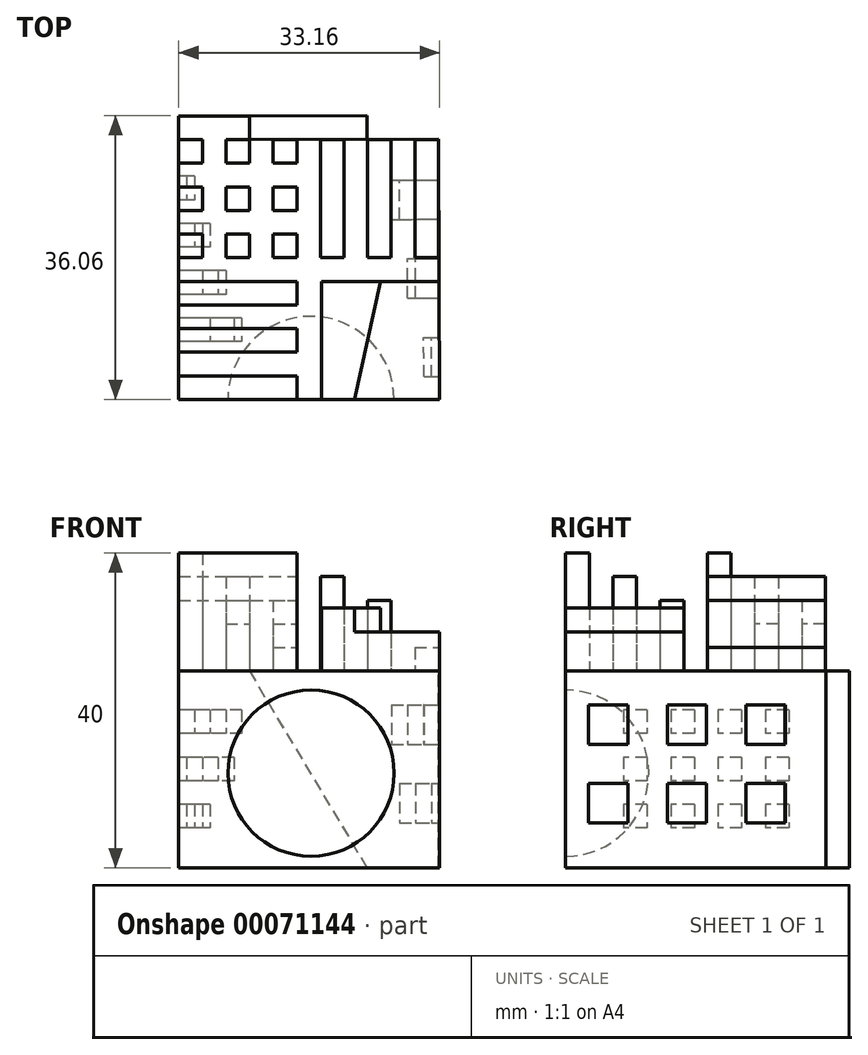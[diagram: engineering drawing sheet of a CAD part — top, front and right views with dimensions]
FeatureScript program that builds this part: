
annotation { "Feature Type Name" : "Feature", "Feature Type Description" : "" }
export const myFeature = defineFeature(function(context is Context, id is Id, definition is map)
    precondition{}
    {
        {
            var Q0;
            Q0=qCreatedBy(makeId("Top.planeOp"),FACE);
            var sketch = newSketch(context, id + "F0", { "sketchPlane" : qUnion([Q0])});
            skLineSegment(sketch, "E0.bottom", {"start": v(-18.94, 29.67) * mm, "end": v(-15.94, 29.67) * mm});
            skLineSegment(sketch, "E0.top", {"start": v(-18.94, 26.67) * mm, "end": v(-15.94, 26.67) * mm});
            skLineSegment(sketch, "E0.left", {"start": v(-18.94, 29.67) * mm, "end": v(-18.94, 26.67) * mm});
            skLineSegment(sketch, "E0.right", {"start": v(-15.94, 29.67) * mm, "end": v(-15.94, 26.67) * mm});
            skLineSegment(sketch, "E1.0.1.0", {"start": v(-18.94, 20.67) * mm, "end": v(-15.94, 20.67) * mm});
            skLineSegment(sketch, "E1.0.1.1", {"start": v(-18.94, 23.67) * mm, "end": v(-18.94, 20.67) * mm});
            skLineSegment(sketch, "E1.0.1.2", {"start": v(-15.94, 23.67) * mm, "end": v(-15.94, 20.67) * mm});
            skLineSegment(sketch, "E1.0.1.3", {"start": v(-18.94, 23.67) * mm, "end": v(-15.94, 23.67) * mm});
            skLineSegment(sketch, "E1.0.2.0", {"start": v(-18.94, 14.67) * mm, "end": v(-15.94, 14.67) * mm});
            skLineSegment(sketch, "E1.0.2.1", {"start": v(-18.94, 17.67) * mm, "end": v(-18.94, 14.67) * mm});
            skLineSegment(sketch, "E1.0.2.2", {"start": v(-15.94, 17.67) * mm, "end": v(-15.94, 14.67) * mm});
            skLineSegment(sketch, "E1.0.2.3", {"start": v(-18.94, 17.67) * mm, "end": v(-15.94, 17.67) * mm});
            skLineSegment(sketch, "E1.1.0.0", {"start": v(-12.94, 26.67) * mm, "end": v(-9.94, 26.67) * mm});
            skLineSegment(sketch, "E1.1.0.1", {"start": v(-12.94, 29.67) * mm, "end": v(-12.94, 26.67) * mm});
            skLineSegment(sketch, "E1.1.0.2", {"start": v(-9.94, 29.67) * mm, "end": v(-9.94, 26.67) * mm});
            skLineSegment(sketch, "E1.1.0.3", {"start": v(-12.94, 29.67) * mm, "end": v(-9.94, 29.67) * mm});
            skLineSegment(sketch, "E1.1.1.0", {"start": v(-12.94, 20.67) * mm, "end": v(-9.94, 20.67) * mm});
            skLineSegment(sketch, "E1.1.1.1", {"start": v(-12.94, 23.67) * mm, "end": v(-12.94, 20.67) * mm});
            skLineSegment(sketch, "E1.1.1.2", {"start": v(-9.94, 23.67) * mm, "end": v(-9.94, 20.67) * mm});
            skLineSegment(sketch, "E1.1.1.3", {"start": v(-12.94, 23.67) * mm, "end": v(-9.94, 23.67) * mm});
            skLineSegment(sketch, "E1.1.2.0", {"start": v(-12.94, 14.67) * mm, "end": v(-9.94, 14.67) * mm});
            skLineSegment(sketch, "E1.1.2.1", {"start": v(-12.94, 17.67) * mm, "end": v(-12.94, 14.67) * mm});
            skLineSegment(sketch, "E1.1.2.2", {"start": v(-9.94, 17.67) * mm, "end": v(-9.94, 14.67) * mm});
            skLineSegment(sketch, "E1.1.2.3", {"start": v(-12.94, 17.67) * mm, "end": v(-9.94, 17.67) * mm});
            skLineSegment(sketch, "E1.2.0.0", {"start": v(-6.94, 26.67) * mm, "end": v(-3.94, 26.67) * mm});
            skLineSegment(sketch, "E1.2.0.1", {"start": v(-6.94, 29.67) * mm, "end": v(-6.94, 26.67) * mm});
            skLineSegment(sketch, "E1.2.0.2", {"start": v(-3.94, 29.67) * mm, "end": v(-3.94, 26.67) * mm});
            skLineSegment(sketch, "E1.2.0.3", {"start": v(-6.94, 29.67) * mm, "end": v(-3.94, 29.67) * mm});
            skLineSegment(sketch, "E1.2.1.0", {"start": v(-6.94, 20.67) * mm, "end": v(-3.94, 20.67) * mm});
            skLineSegment(sketch, "E1.2.1.1", {"start": v(-6.94, 23.67) * mm, "end": v(-6.94, 20.67) * mm});
            skLineSegment(sketch, "E1.2.1.2", {"start": v(-3.94, 23.67) * mm, "end": v(-3.94, 20.67) * mm});
            skLineSegment(sketch, "E1.2.1.3", {"start": v(-6.94, 23.67) * mm, "end": v(-3.94, 23.67) * mm});
            skLineSegment(sketch, "E1.2.2.0", {"start": v(-6.94, 14.67) * mm, "end": v(-3.94, 14.67) * mm});
            skLineSegment(sketch, "E1.2.2.1", {"start": v(-6.94, 17.67) * mm, "end": v(-6.94, 14.67) * mm});
            skLineSegment(sketch, "E1.2.2.2", {"start": v(-3.94, 17.67) * mm, "end": v(-3.94, 14.67) * mm});
            skLineSegment(sketch, "E1.2.2.3", {"start": v(-6.94, 17.67) * mm, "end": v(-3.94, 17.67) * mm});
            skLineSegment(sketch, "E1.direction2", {"start": v(-18.94, 26.67) * mm, "end": v(-18.94, 20.67) * mm, "construction": true});
            skLineSegment(sketch, "E2.bottom", {"start": v(-0.94, 29.67) * mm, "end": v(2.06, 29.67) * mm});
            skLineSegment(sketch, "E2.top", {"start": v(-0.94, 14.67) * mm, "end": v(2.06, 14.67) * mm});
            skLineSegment(sketch, "E2.left", {"start": v(-0.94, 29.67) * mm, "end": v(-0.94, 14.67) * mm});
            skLineSegment(sketch, "E2.right", {"start": v(2.06, 29.67) * mm, "end": v(2.06, 14.67) * mm});
            skLineSegment(sketch, "E3.0.1.0", {"start": v(-0.94, 29.75) * mm, "end": v(2.06, 29.75) * mm});
            skLineSegment(sketch, "E3.0.1.1", {"start": v(-0.94, 29.75) * mm, "end": v(-0.94, 14.75) * mm});
            skLineSegment(sketch, "E3.0.1.2", {"start": v(2.06, 29.75) * mm, "end": v(2.06, 14.75) * mm});
            skLineSegment(sketch, "E3.1.0.0", {"start": v(5.06, 29.67) * mm, "end": v(8.06, 29.67) * mm});
            skLineSegment(sketch, "E3.1.0.1", {"start": v(5.06, 29.67) * mm, "end": v(5.06, 14.67) * mm});
            skLineSegment(sketch, "E3.1.0.2", {"start": v(8.06, 29.67) * mm, "end": v(8.06, 14.67) * mm});
            skLineSegment(sketch, "E3.1.0.3", {"start": v(5.06, 14.67) * mm, "end": v(8.06, 14.67) * mm});
            skLineSegment(sketch, "E3.1.1.0", {"start": v(5.06, 29.75) * mm, "end": v(8.06, 29.75) * mm});
            skLineSegment(sketch, "E3.1.1.1", {"start": v(5.06, 29.75) * mm, "end": v(5.06, 14.75) * mm});
            skLineSegment(sketch, "E3.1.1.2", {"start": v(8.06, 29.75) * mm, "end": v(8.06, 14.75) * mm});
            skLineSegment(sketch, "E3.2.0.0", {"start": v(11.06, 29.67) * mm, "end": v(14.06, 29.67) * mm});
            skLineSegment(sketch, "E3.2.0.1", {"start": v(11.06, 29.67) * mm, "end": v(11.06, 14.67) * mm});
            skLineSegment(sketch, "E3.2.0.2", {"start": v(14.06, 29.67) * mm, "end": v(14.06, 14.67) * mm});
            skLineSegment(sketch, "E3.2.0.3", {"start": v(11.06, 14.67) * mm, "end": v(14.06, 14.67) * mm});
            skLineSegment(sketch, "E3.2.1.0", {"start": v(11.06, 29.75) * mm, "end": v(14.06, 29.75) * mm});
            skLineSegment(sketch, "E3.2.1.1", {"start": v(11.06, 29.75) * mm, "end": v(11.06, 14.75) * mm});
            skLineSegment(sketch, "E3.2.1.2", {"start": v(14.06, 29.75) * mm, "end": v(14.06, 14.75) * mm});
            skLineSegment(sketch, "E3.direction1", {"start": v(-0.94, 29.67) * mm, "end": v(5.06, 29.67) * mm, "construction": true});
            skLineSegment(sketch, "E3.direction2", {"start": v(-0.94, 29.67) * mm, "end": v(-0.94, 29.75) * mm, "construction": true});
            skLineSegment(sketch, "E4.bottom", {"start": v(-18.94, 11.67) * mm, "end": v(-3.94, 11.67) * mm});
            skLineSegment(sketch, "E4.top", {"start": v(-18.94, 8.67) * mm, "end": v(-3.94, 8.67) * mm});
            skLineSegment(sketch, "E4.left", {"start": v(-18.94, 11.67) * mm, "end": v(-18.94, 8.67) * mm});
            skLineSegment(sketch, "E4.right", {"start": v(-3.94, 11.67) * mm, "end": v(-3.94, 8.67) * mm});
            skLineSegment(sketch, "E5.0.1.0", {"start": v(-18.94, 5.67) * mm, "end": v(-3.94, 5.67) * mm});
            skLineSegment(sketch, "E5.0.1.1", {"start": v(-18.94, 5.67) * mm, "end": v(-18.94, 2.67) * mm});
            skLineSegment(sketch, "E5.0.1.2", {"start": v(-18.94, 2.67) * mm, "end": v(-3.94, 2.67) * mm});
            skLineSegment(sketch, "E5.0.1.3", {"start": v(-3.94, 5.67) * mm, "end": v(-3.94, 2.67) * mm});
            skLineSegment(sketch, "E5.0.2.0", {"start": v(-18.94, -0.33) * mm, "end": v(-3.94, -0.33) * mm});
            skLineSegment(sketch, "E5.0.2.1", {"start": v(-18.94, -0.33) * mm, "end": v(-18.94, -3.33) * mm});
            skLineSegment(sketch, "E5.0.2.2", {"start": v(-18.94, -3.33) * mm, "end": v(-3.94, -3.33) * mm});
            skLineSegment(sketch, "E5.0.2.3", {"start": v(-3.94, -0.33) * mm, "end": v(-3.94, -3.33) * mm});
            skLineSegment(sketch, "E5.direction2", {"start": v(-18.94, 11.67) * mm, "end": v(-18.94, 5.67) * mm, "construction": true});
            skLineSegment(sketch, "E6.bottom", {"start": v(14.22, -3.33) * mm, "end": v(-0.78, -3.33) * mm});
            skLineSegment(sketch, "E6.top", {"start": v(14.22, 11.67) * mm, "end": v(-0.78, 11.67) * mm});
            skLineSegment(sketch, "E6.left", {"start": v(14.22, -3.33) * mm, "end": v(14.22, 11.67) * mm});
            skLineSegment(sketch, "E6.right", {"start": v(-0.78, -3.33) * mm, "end": v(-0.78, 11.67) * mm});
            skLineSegment(sketch, "E7", {"start": v(-18.94, 29.67) * mm, "end": v(14.06, 29.75) * mm});
            skLineSegment(sketch, "E8", {"start": v(14.06, 29.75) * mm, "end": v(14.22, -3.33) * mm});
            skLineSegment(sketch, "E9", {"start": v(14.22, -3.33) * mm, "end": v(-18.94, -3.33) * mm});
            skLineSegment(sketch, "E10", {"start": v(-18.94, 29.67) * mm, "end": v(-18.94, -3.33) * mm});
            skSolve(sketch);
        }
        {
            var Q0;
            {var subQ0=sQuery(id+"F0.wireOp",EDGE,"E6.right");Q0=makeQuery(id+"F0.imprint","IMPRINT",FACE,{"disambiguationData":[TD([[makeQuery(id+"F0.imprint","IMPRINT",EDGE,{"derivedFrom":subQ0}),-1.0]])]});}
            extrude(context, id + "F1", {"entities" : qUnion([Q0]), "depth" : 5 * mm});
        }
        {
            var Q0;
            {var subQ0=sQuery(id+"F0.wireOp",EDGE,"E5.0.2.0");Q0=makeQuery(id+"F0.imprint","IMPRINT",FACE,{"disambiguationData":[TD([[makeQuery(id+"F0.imprint","IMPRINT",EDGE,{"derivedFrom":subQ0}),-1.0]])]});}
            extrude(context, id + "F2", {"entities" : qUnion([Q0]), "depth" : 15 * mm});
        }
        {
            var Q0;
            Q0=makeQuery(id+"F0.imprint","IMPRINT",FACE,{"disambiguationData":[TD([[makeQuery(id+"F0.imprint","IMPRINT",EDGE,{"derivedFrom":sQuery(id+"F0.wireOp",EDGE,"E1.2.0.0")}),1.0]])]});
            extrude(context, id + "F3", {"entities" : qUnion([Q0]), "depth" : 3 * mm});
        }
        {
            var Q0;
            {var subQ2=sQuery(id+"F0.wireOp",EDGE,"E2.bottom");Q0=makeQuery(id+"F0.imprint","IMPRINT",FACE,{"disambiguationData":[TD([[makeQuery(id+"F0.imprint","IMPRINT",EDGE,{"derivedFrom":subQ2}),-1.0]])]});}
            extrude(context, id + "F4", {"entities" : qUnion([Q0]), "depth" : 12 * mm});
        }
        {
            var Q0;
            Q0=qCreatedBy(makeId("Top.planeOp"),FACE);
            var sketch = newSketch(context, id + "F5", { "sketchPlane" : qUnion([Q0])});
            skLineSegment(sketch, "E11.0", {"start": v(14.22, -3.33) * mm, "end": v(-18.94, -3.33) * mm});
            skLineSegment(sketch, "E12.0", {"start": v(-18.94, 29.67) * mm, "end": v(-18.94, -3.33) * mm});
            skLineSegment(sketch, "E13.0", {"start": v(14.06, 29.75) * mm, "end": v(14.22, -3.33) * mm});
            skLineSegment(sketch, "E14.0", {"start": v(-18.94, 29.67) * mm, "end": v(14.06, 29.75) * mm});
            skSolve(sketch);
        }
        {
            var Q0;
            Q0=makeQuery(id+"F5.imprint","IMPRINT",FACE,{"disambiguationData":[TD([[makeQuery(id+"F5.imprint","IMPRINT",EDGE,{"derivedFrom":sQuery(id+"F5.wireOp",EDGE,"E11.0")}),-1.0]])]});
            extrude(context, id + "F6", {"entities" : qUnion([Q0]), "oppositeDirection" : true, "depth" : 25 * mm});
        }
        {
            var Q0;
            Q0=makeQuery(id+"F6.opExtrude","SWEPT_FACE",FACE,{"disambiguationData":[OSD([sQuery(id+"F5.wireOp",EDGE,"E11.0")])]});
            var sketch = newSketch(context, id + "F7", { "sketchPlane" : qUnion([Q0])});
            skCircle(sketch, "E15", {"center": v(-2.12, -12.97) * mm, "radius": 10.56 * mm});
            skLineSegment(sketch, "E16", {"start": v(-2.12, -2.4) * mm, "end": v(-2.12, -23.53) * mm});
            skSolve(sketch);
        }
        {
            var Q0;
            {var subQ0=sQuery(id+"F7.wireOp",EDGE,"E16");Q0=makeQuery(id+"F7.imprint","IMPRINT",FACE,{"disambiguationData":[TD([[makeQuery(id+"F7.imprint","IMPRINT",EDGE,{"derivedFrom":subQ0}),-1.0]])]});}
            var Q1;
            Q1=sQuery(id+"F7.wireOp",EDGE,"E16");
            revolve(context, id + "F8", {"operationType" : NewBodyOperationType.REMOVE, "entities" : qUnion([Q0]), "axis" : qUnion([Q1]), "revolveType" : RevolveType.FULL, "oppositeDirection" : true});
        }
        {
            var Q0;
            Q0=makeQuery(id+"F6.opExtrude","SWEPT_FACE",FACE,{"disambiguationData":[OSD([sQuery(id+"F5.wireOp",EDGE,"E12.0")])]});
            var sketch = newSketch(context, id + "F9", { "sketchPlane" : qUnion([Q0])});
            skLineSegment(sketch, "E17.bottom", {"start": v(-25.02, -4.95) * mm, "end": v(-22.02, -4.95) * mm});
            skLineSegment(sketch, "E17.top", {"start": v(-25.02, -7.95) * mm, "end": v(-22.02, -7.95) * mm});
            skLineSegment(sketch, "E17.left", {"start": v(-25.02, -4.95) * mm, "end": v(-25.02, -7.95) * mm});
            skLineSegment(sketch, "E17.right", {"start": v(-22.02, -4.95) * mm, "end": v(-22.02, -7.95) * mm});
            skLineSegment(sketch, "E18.0.1.0", {"start": v(-25.02, -10.95) * mm, "end": v(-25.02, -13.95) * mm});
            skLineSegment(sketch, "E18.0.1.1", {"start": v(-25.02, -13.95) * mm, "end": v(-22.02, -13.95) * mm});
            skLineSegment(sketch, "E18.0.1.2", {"start": v(-25.02, -10.95) * mm, "end": v(-22.02, -10.95) * mm});
            skLineSegment(sketch, "E18.0.1.3", {"start": v(-22.02, -10.95) * mm, "end": v(-22.02, -13.95) * mm});
            skLineSegment(sketch, "E18.0.2.0", {"start": v(-25.02, -16.95) * mm, "end": v(-25.02, -19.95) * mm});
            skLineSegment(sketch, "E18.0.2.1", {"start": v(-25.02, -19.95) * mm, "end": v(-22.02, -19.95) * mm});
            skLineSegment(sketch, "E18.0.2.2", {"start": v(-25.02, -16.95) * mm, "end": v(-22.02, -16.95) * mm});
            skLineSegment(sketch, "E18.0.2.3", {"start": v(-22.02, -16.95) * mm, "end": v(-22.02, -19.95) * mm});
            skLineSegment(sketch, "E18.1.0.0", {"start": v(-19.02, -4.95) * mm, "end": v(-19.02, -7.95) * mm});
            skLineSegment(sketch, "E18.1.0.1", {"start": v(-19.02, -7.95) * mm, "end": v(-16.02, -7.95) * mm});
            skLineSegment(sketch, "E18.1.0.2", {"start": v(-19.02, -4.95) * mm, "end": v(-16.02, -4.95) * mm});
            skLineSegment(sketch, "E18.1.0.3", {"start": v(-16.02, -4.95) * mm, "end": v(-16.02, -7.95) * mm});
            skLineSegment(sketch, "E18.1.1.0", {"start": v(-19.02, -10.95) * mm, "end": v(-19.02, -13.95) * mm});
            skLineSegment(sketch, "E18.1.1.1", {"start": v(-19.02, -13.95) * mm, "end": v(-16.02, -13.95) * mm});
            skLineSegment(sketch, "E18.1.1.2", {"start": v(-19.02, -10.95) * mm, "end": v(-16.02, -10.95) * mm});
            skLineSegment(sketch, "E18.1.1.3", {"start": v(-16.02, -10.95) * mm, "end": v(-16.02, -13.95) * mm});
            skLineSegment(sketch, "E18.1.2.0", {"start": v(-19.02, -16.95) * mm, "end": v(-19.02, -19.95) * mm});
            skLineSegment(sketch, "E18.1.2.1", {"start": v(-19.02, -19.95) * mm, "end": v(-16.02, -19.95) * mm});
            skLineSegment(sketch, "E18.1.2.2", {"start": v(-19.02, -16.95) * mm, "end": v(-16.02, -16.95) * mm});
            skLineSegment(sketch, "E18.1.2.3", {"start": v(-16.02, -16.95) * mm, "end": v(-16.02, -19.95) * mm});
            skLineSegment(sketch, "E18.2.0.0", {"start": v(-13.02, -4.95) * mm, "end": v(-13.02, -7.95) * mm});
            skLineSegment(sketch, "E18.2.0.1", {"start": v(-13.02, -7.95) * mm, "end": v(-10.02, -7.95) * mm});
            skLineSegment(sketch, "E18.2.0.2", {"start": v(-13.02, -4.95) * mm, "end": v(-10.02, -4.95) * mm});
            skLineSegment(sketch, "E18.2.0.3", {"start": v(-10.02, -4.95) * mm, "end": v(-10.02, -7.95) * mm});
            skLineSegment(sketch, "E18.2.1.0", {"start": v(-13.02, -10.95) * mm, "end": v(-13.02, -13.95) * mm});
            skLineSegment(sketch, "E18.2.1.1", {"start": v(-13.02, -13.95) * mm, "end": v(-10.02, -13.95) * mm});
            skLineSegment(sketch, "E18.2.1.2", {"start": v(-13.02, -10.95) * mm, "end": v(-10.02, -10.95) * mm});
            skLineSegment(sketch, "E18.2.1.3", {"start": v(-10.02, -10.95) * mm, "end": v(-10.02, -13.95) * mm});
            skLineSegment(sketch, "E18.2.2.0", {"start": v(-13.02, -16.95) * mm, "end": v(-13.02, -19.95) * mm});
            skLineSegment(sketch, "E18.2.2.1", {"start": v(-13.02, -19.95) * mm, "end": v(-10.02, -19.95) * mm});
            skLineSegment(sketch, "E18.2.2.2", {"start": v(-13.02, -16.95) * mm, "end": v(-10.02, -16.95) * mm});
            skLineSegment(sketch, "E18.2.2.3", {"start": v(-10.02, -16.95) * mm, "end": v(-10.02, -19.95) * mm});
            skLineSegment(sketch, "E18.3.0.0", {"start": v(-7.02, -4.95) * mm, "end": v(-7.02, -7.95) * mm});
            skLineSegment(sketch, "E18.3.0.1", {"start": v(-7.02, -7.95) * mm, "end": v(-4.02, -7.95) * mm});
            skLineSegment(sketch, "E18.3.0.2", {"start": v(-7.02, -4.95) * mm, "end": v(-4.02, -4.95) * mm});
            skLineSegment(sketch, "E18.3.0.3", {"start": v(-4.02, -4.95) * mm, "end": v(-4.02, -7.95) * mm});
            skLineSegment(sketch, "E18.3.1.0", {"start": v(-7.02, -10.95) * mm, "end": v(-7.02, -13.95) * mm});
            skLineSegment(sketch, "E18.3.1.1", {"start": v(-7.02, -13.95) * mm, "end": v(-4.02, -13.95) * mm});
            skLineSegment(sketch, "E18.3.1.2", {"start": v(-7.02, -10.95) * mm, "end": v(-4.02, -10.95) * mm});
            skLineSegment(sketch, "E18.3.1.3", {"start": v(-4.02, -10.95) * mm, "end": v(-4.02, -13.95) * mm});
            skLineSegment(sketch, "E18.3.2.0", {"start": v(-7.02, -16.95) * mm, "end": v(-7.02, -19.95) * mm});
            skLineSegment(sketch, "E18.3.2.1", {"start": v(-7.02, -19.95) * mm, "end": v(-4.02, -19.95) * mm});
            skLineSegment(sketch, "E18.3.2.2", {"start": v(-7.02, -16.95) * mm, "end": v(-4.02, -16.95) * mm});
            skLineSegment(sketch, "E18.3.2.3", {"start": v(-4.02, -16.95) * mm, "end": v(-4.02, -19.95) * mm});
            skLineSegment(sketch, "E18.direction1", {"start": v(-25.02, -7.95) * mm, "end": v(-19.02, -7.95) * mm, "construction": true});
            skLineSegment(sketch, "E18.direction2", {"start": v(-25.02, -7.95) * mm, "end": v(-25.02, -13.95) * mm, "construction": true});
            skSolve(sketch);
        }
        {
            var Q0;
            Q0=makeQuery(id+"F6.opExtrude","SWEPT_FACE",FACE,{"disambiguationData":[OSD([sQuery(id+"F5.wireOp",EDGE,"E13.0")])]});
            var sketch = newSketch(context, id + "F10", { "sketchPlane" : qUnion([Q0])});
            skLineSegment(sketch, "E19.bottom", {"start": v(-0.5, -4.3) * mm, "end": v(4.5, -4.3) * mm});
            skLineSegment(sketch, "E19.top", {"start": v(-0.5, -9.3) * mm, "end": v(4.5, -9.3) * mm});
            skLineSegment(sketch, "E19.left", {"start": v(-0.5, -4.3) * mm, "end": v(-0.5, -9.3) * mm});
            skLineSegment(sketch, "E19.right", {"start": v(4.5, -4.3) * mm, "end": v(4.5, -9.3) * mm});
            skLineSegment(sketch, "E20.0.1.0", {"start": v(-0.5, -14.3) * mm, "end": v(4.5, -14.3) * mm});
            skLineSegment(sketch, "E20.0.1.1", {"start": v(-0.5, -19.3) * mm, "end": v(4.5, -19.3) * mm});
            skLineSegment(sketch, "E20.0.1.2", {"start": v(4.5, -14.3) * mm, "end": v(4.5, -19.3) * mm});
            skLineSegment(sketch, "E20.0.1.3", {"start": v(-0.5, -14.3) * mm, "end": v(-0.5, -19.3) * mm});
            skLineSegment(sketch, "E20.1.0.0", {"start": v(9.5, -4.3) * mm, "end": v(14.5, -4.3) * mm});
            skLineSegment(sketch, "E20.1.0.1", {"start": v(9.5, -9.3) * mm, "end": v(14.5, -9.3) * mm});
            skLineSegment(sketch, "E20.1.0.2", {"start": v(14.5, -4.3) * mm, "end": v(14.5, -9.3) * mm});
            skLineSegment(sketch, "E20.1.0.3", {"start": v(9.5, -4.3) * mm, "end": v(9.5, -9.3) * mm});
            skLineSegment(sketch, "E20.1.1.0", {"start": v(9.5, -14.3) * mm, "end": v(14.5, -14.3) * mm});
            skLineSegment(sketch, "E20.1.1.1", {"start": v(9.5, -19.3) * mm, "end": v(14.5, -19.3) * mm});
            skLineSegment(sketch, "E20.1.1.2", {"start": v(14.5, -14.3) * mm, "end": v(14.5, -19.3) * mm});
            skLineSegment(sketch, "E20.1.1.3", {"start": v(9.5, -14.3) * mm, "end": v(9.5, -19.3) * mm});
            skLineSegment(sketch, "E20.2.0.0", {"start": v(19.5, -4.3) * mm, "end": v(24.5, -4.3) * mm});
            skLineSegment(sketch, "E20.2.0.1", {"start": v(19.5, -9.3) * mm, "end": v(24.5, -9.3) * mm});
            skLineSegment(sketch, "E20.2.0.2", {"start": v(24.5, -4.3) * mm, "end": v(24.5, -9.3) * mm});
            skLineSegment(sketch, "E20.2.0.3", {"start": v(19.5, -4.3) * mm, "end": v(19.5, -9.3) * mm});
            skLineSegment(sketch, "E20.2.1.0", {"start": v(19.5, -14.3) * mm, "end": v(24.5, -14.3) * mm});
            skLineSegment(sketch, "E20.2.1.1", {"start": v(19.5, -19.3) * mm, "end": v(24.5, -19.3) * mm});
            skLineSegment(sketch, "E20.2.1.2", {"start": v(24.5, -14.3) * mm, "end": v(24.5, -19.3) * mm});
            skLineSegment(sketch, "E20.2.1.3", {"start": v(19.5, -14.3) * mm, "end": v(19.5, -19.3) * mm});
            skLineSegment(sketch, "E20.direction1", {"start": v(-0.5, -4.3) * mm, "end": v(9.5, -4.3) * mm, "construction": true});
            skLineSegment(sketch, "E20.direction2", {"start": v(-0.5, -4.3) * mm, "end": v(-0.5, -14.3) * mm, "construction": true});
            skSolve(sketch);
        }
        {
            var Q0;
            Q0=makeQuery(id+"F10.imprint","IMPRINT",FACE,{"disambiguationData":[TD([[makeQuery(id+"F10.imprint","IMPRINT",EDGE,{"derivedFrom":sQuery(id+"F10.wireOp",EDGE,"E19.bottom")}),-1.0]])]});
            extrude(context, id + "F11", {"entities" : qUnion([Q0]), "operationType" : NewBodyOperationType.REMOVE, "oppositeDirection" : true, "depth" : 2 * mm});
        }
        {
            var Q0;
            {var subQ0=sQuery(id+"F0.wireOp",EDGE,"E5.0.1.0");Q0=makeQuery(id+"F0.imprint","IMPRINT",FACE,{"disambiguationData":[TD([[makeQuery(id+"F0.imprint","IMPRINT",EDGE,{"derivedFrom":subQ0}),-1.0]])]});}
            extrude(context, id + "F12", {"entities" : qUnion([Q0]), "operationType" : NewBodyOperationType.ADD, "depth" : 12 * mm});
        }
        {
            var Q0;
            {var subQ0=sQuery(id+"F0.wireOp",EDGE,"E4.bottom");Q0=makeQuery(id+"F0.imprint","IMPRINT",FACE,{"disambiguationData":[TD([[makeQuery(id+"F0.imprint","IMPRINT",EDGE,{"derivedFrom":subQ0}),-1.0]])]});}
            extrude(context, id + "F13", {"entities" : qUnion([Q0]), "operationType" : NewBodyOperationType.ADD, "depth" : 9 * mm});
        }
        {
            var Q0;
            Q0=makeQuery(id+"F0.imprint","IMPRINT",FACE,{"disambiguationData":[TD([[makeQuery(id+"F0.imprint","IMPRINT",EDGE,{"derivedFrom":sQuery(id+"F0.wireOp",EDGE,"E1.1.0.0")}),1.0]])]});
            extrude(context, id + "F14", {"entities" : qUnion([Q0]), "operationType" : NewBodyOperationType.ADD, "depth" : 6 * mm});
        }
        {
            var Q0;
            {var subQ0=sQuery(id+"F0.wireOp",EDGE,"E0.bottom");Q0=makeQuery(id+"F0.imprint","IMPRINT",FACE,{"disambiguationData":[TD([[makeQuery(id+"F0.imprint","IMPRINT",EDGE,{"derivedFrom":subQ0}),-1.0]])]});}
            extrude(context, id + "F15", {"entities" : qUnion([Q0]), "operationType" : NewBodyOperationType.ADD, "depth" : 9 * mm});
        }
        {
            var Q0;
            Q0=makeQuery(id+"F0.imprint","IMPRINT",FACE,{"disambiguationData":[TD([[makeQuery(id+"F0.imprint","IMPRINT",EDGE,{"derivedFrom":sQuery(id+"F0.wireOp",EDGE,"E1.1.1.0")}),1.0]])]});
            extrude(context, id + "F16", {"entities" : qUnion([Q0]), "operationType" : NewBodyOperationType.ADD, "depth" : 9 * mm});
        }
        {
            var Q0;
            {var subQ0=sQuery(id+"F0.wireOp",EDGE,"E1.0.2.0");Q0=makeQuery(id+"F0.imprint","IMPRINT",FACE,{"disambiguationData":[TD([[makeQuery(id+"F0.imprint","IMPRINT",EDGE,{"derivedFrom":subQ0}),1.0]])]});}
            extrude(context, id + "F17", {"entities" : qUnion([Q0]), "operationType" : NewBodyOperationType.ADD, "depth" : 15 * mm});
        }
        {
            var Q0;
            {var subQ0=sQuery(id+"F0.wireOp",EDGE,"E1.0.1.0");Q0=makeQuery(id+"F0.imprint","IMPRINT",FACE,{"disambiguationData":[TD([[makeQuery(id+"F0.imprint","IMPRINT",EDGE,{"derivedFrom":subQ0}),1.0]])]});}
            extrude(context, id + "F18", {"entities" : qUnion([Q0]), "operationType" : NewBodyOperationType.ADD, "depth" : 12 * mm});
        }
        {
            var Q0;
            Q0=makeQuery(id+"F0.imprint","IMPRINT",FACE,{"disambiguationData":[TD([[makeQuery(id+"F0.imprint","IMPRINT",EDGE,{"derivedFrom":sQuery(id+"F0.wireOp",EDGE,"E1.2.1.0")}),1.0]])]});
            extrude(context, id + "F19", {"entities" : qUnion([Q0]), "operationType" : NewBodyOperationType.ADD, "depth" : 6 * mm});
        }
        {
            var Q0;
            Q0=makeQuery(id+"F0.imprint","IMPRINT",FACE,{"disambiguationData":[TD([[makeQuery(id+"F0.imprint","IMPRINT",EDGE,{"derivedFrom":sQuery(id+"F0.wireOp",EDGE,"E1.2.2.0")}),1.0]])]});
            extrude(context, id + "F20", {"entities" : qUnion([Q0]), "operationType" : NewBodyOperationType.ADD, "depth" : 9 * mm});
        }
        {
            var Q0;
            Q0=makeQuery(id+"F0.imprint","IMPRINT",FACE,{"disambiguationData":[TD([[makeQuery(id+"F0.imprint","IMPRINT",EDGE,{"derivedFrom":sQuery(id+"F0.wireOp",EDGE,"E1.1.2.0")}),1.0]])]});
            extrude(context, id + "F21", {"entities" : qUnion([Q0]), "operationType" : NewBodyOperationType.ADD, "depth" : 12 * mm});
        }
        {
            var Q0;
            {var subQ1=sQuery(id+"F0.wireOp",EDGE,"E3.1.0.0");Q0=makeQuery(id+"F0.imprint","IMPRINT",FACE,{"disambiguationData":[TD([[makeQuery(id+"F0.imprint","IMPRINT",EDGE,{"derivedFrom":subQ1}),-1.0]])]});}
            extrude(context, id + "F22", {"entities" : qUnion([Q0]), "operationType" : NewBodyOperationType.ADD, "depth" : 9 * mm});
        }
        {
            var Q0;
            {var subQ2=sQuery(id+"F0.wireOp",EDGE,"E3.2.0.0");Q0=makeQuery(id+"F0.imprint","IMPRINT",FACE,{"disambiguationData":[TD([[makeQuery(id+"F0.imprint","IMPRINT",EDGE,{"derivedFrom":subQ2}),-1.0]])]});}
            extrude(context, id + "F23", {"entities" : qUnion([Q0]), "operationType" : NewBodyOperationType.ADD, "depth" : 3 * mm});
        }
        {
            var Q0;
            Q0=makeQuery(id+"F10.imprint","IMPRINT",FACE,{"disambiguationData":[TD([[makeQuery(id+"F10.imprint","IMPRINT",EDGE,{"derivedFrom":sQuery(id+"F10.wireOp",EDGE,"E20.1.0.0")}),-1.0]])]});
            extrude(context, id + "F24", {"entities" : qUnion([Q0]), "operationType" : NewBodyOperationType.REMOVE, "oppositeDirection" : true, "depth" : 4 * mm});
        }
        {
            var Q0;
            Q0=makeQuery(id+"F10.imprint","IMPRINT",FACE,{"disambiguationData":[TD([[makeQuery(id+"F10.imprint","IMPRINT",EDGE,{"derivedFrom":sQuery(id+"F10.wireOp",EDGE,"E20.2.0.0")}),-1.0]])]});
            extrude(context, id + "F25", {"entities" : qUnion([Q0]), "operationType" : NewBodyOperationType.REMOVE, "oppositeDirection" : true, "depth" : 6 * mm});
        }
        {
            var Q0;
            Q0=makeQuery(id+"F10.imprint","IMPRINT",FACE,{"disambiguationData":[TD([[makeQuery(id+"F10.imprint","IMPRINT",EDGE,{"derivedFrom":sQuery(id+"F10.wireOp",EDGE,"E20.0.1.0")}),-1.0]])]});
            extrude(context, id + "F26", {"entities" : qUnion([Q0]), "operationType" : NewBodyOperationType.REMOVE, "oppositeDirection" : true, "depth" : 1 * mm});
        }
        {
            var Q0;
            Q0=makeQuery(id+"F10.imprint","IMPRINT",FACE,{"disambiguationData":[TD([[makeQuery(id+"F10.imprint","IMPRINT",EDGE,{"derivedFrom":sQuery(id+"F10.wireOp",EDGE,"E20.1.1.0")}),-1.0]])]});
            extrude(context, id + "F27", {"entities" : qUnion([Q0]), "operationType" : NewBodyOperationType.REMOVE, "oppositeDirection" : true, "depth" : 3 * mm});
        }
        {
            var Q0;
            Q0=makeQuery(id+"F10.imprint","IMPRINT",FACE,{"disambiguationData":[TD([[makeQuery(id+"F10.imprint","IMPRINT",EDGE,{"derivedFrom":sQuery(id+"F10.wireOp",EDGE,"E20.2.1.0")}),-1.0]])]});
            extrude(context, id + "F28", {"entities" : qUnion([Q0]), "operationType" : NewBodyOperationType.REMOVE, "oppositeDirection" : true, "depth" : 5 * mm});
        }
        {
            var Q0;
            Q0=makeQuery(id+"F9.imprint","IMPRINT",FACE,{"disambiguationData":[TD([[makeQuery(id+"F9.imprint","IMPRINT",EDGE,{"derivedFrom":sQuery(id+"F9.wireOp",EDGE,"E17.bottom")}),-1.0]])]});
            extrude(context, id + "F29", {"entities" : qUnion([Q0]), "operationType" : NewBodyOperationType.REMOVE, "oppositeDirection" : true, "depth" : 2 * mm});
        }
        {
            var Q0;
            Q0=makeQuery(id+"F9.imprint","IMPRINT",FACE,{"disambiguationData":[TD([[makeQuery(id+"F9.imprint","IMPRINT",EDGE,{"derivedFrom":sQuery(id+"F9.wireOp",EDGE,"E18.1.0.0")}),1.0]])]});
            extrude(context, id + "F30", {"entities" : qUnion([Q0]), "operationType" : NewBodyOperationType.REMOVE, "oppositeDirection" : true, "depth" : 4 * mm});
        }
        {
            var Q0;
            Q0=makeQuery(id+"F9.imprint","IMPRINT",FACE,{"disambiguationData":[TD([[makeQuery(id+"F9.imprint","IMPRINT",EDGE,{"derivedFrom":sQuery(id+"F9.wireOp",EDGE,"E18.2.0.0")}),1.0]])]});
            extrude(context, id + "F31", {"entities" : qUnion([Q0]), "operationType" : NewBodyOperationType.REMOVE, "oppositeDirection" : true, "depth" : 6 * mm});
        }
        {
            var Q0;
            Q0=makeQuery(id+"F9.imprint","IMPRINT",FACE,{"disambiguationData":[TD([[makeQuery(id+"F9.imprint","IMPRINT",EDGE,{"derivedFrom":sQuery(id+"F9.wireOp",EDGE,"E18.3.0.0")}),1.0]])]});
            extrude(context, id + "F32", {"entities" : qUnion([Q0]), "operationType" : NewBodyOperationType.REMOVE, "oppositeDirection" : true, "depth" : 8 * mm});
        }
        {
            var Q0;
            Q0=makeQuery(id+"F9.imprint","IMPRINT",FACE,{"disambiguationData":[TD([[makeQuery(id+"F9.imprint","IMPRINT",EDGE,{"derivedFrom":sQuery(id+"F9.wireOp",EDGE,"E18.0.1.0")}),1.0]])]});
            extrude(context, id + "F33", {"entities" : qUnion([Q0]), "operationType" : NewBodyOperationType.REMOVE, "oppositeDirection" : true, "depth" : 1 * mm});
        }
        {
            var Q0;
            Q0=makeQuery(id+"F9.imprint","IMPRINT",FACE,{"disambiguationData":[TD([[makeQuery(id+"F9.imprint","IMPRINT",EDGE,{"derivedFrom":sQuery(id+"F9.wireOp",EDGE,"E18.1.1.0")}),1.0]])]});
            extrude(context, id + "F34", {"entities" : qUnion([Q0]), "operationType" : NewBodyOperationType.REMOVE, "oppositeDirection" : true, "depth" : 3 * mm});
        }
        {
            var Q0;
            Q0=makeQuery(id+"F9.imprint","IMPRINT",FACE,{"disambiguationData":[TD([[makeQuery(id+"F9.imprint","IMPRINT",EDGE,{"derivedFrom":sQuery(id+"F9.wireOp",EDGE,"E18.2.1.0")}),1.0]])]});
            extrude(context, id + "F35", {"entities" : qUnion([Q0]), "operationType" : NewBodyOperationType.REMOVE, "oppositeDirection" : true, "depth" : 5 * mm});
        }
        {
            var Q0;
            Q0=makeQuery(id+"F9.imprint","IMPRINT",FACE,{"disambiguationData":[TD([[makeQuery(id+"F9.imprint","IMPRINT",EDGE,{"derivedFrom":sQuery(id+"F9.wireOp",EDGE,"E18.3.1.0")}),1.0]])]});
            extrude(context, id + "F36", {"entities" : qUnion([Q0]), "operationType" : NewBodyOperationType.REMOVE, "oppositeDirection" : true, "depth" : 7 * mm});
        }
        {
            var Q0;
            Q0=makeQuery(id+"F9.imprint","IMPRINT",FACE,{"disambiguationData":[TD([[makeQuery(id+"F9.imprint","IMPRINT",EDGE,{"derivedFrom":sQuery(id+"F9.wireOp",EDGE,"E18.0.2.0")}),1.0]])]});
            extrude(context, id + "F37", {"entities" : qUnion([Q0]), "operationType" : NewBodyOperationType.REMOVE, "oppositeDirection" : true, "depth" : 1 * mm});
        }
        {
            var Q0;
            Q0=makeQuery(id+"F9.imprint","IMPRINT",FACE,{"disambiguationData":[TD([[makeQuery(id+"F9.imprint","IMPRINT",EDGE,{"derivedFrom":sQuery(id+"F9.wireOp",EDGE,"E18.1.2.0")}),1.0]])]});
            extrude(context, id + "F38", {"entities" : qUnion([Q0]), "operationType" : NewBodyOperationType.REMOVE, "oppositeDirection" : true, "depth" : 2 * mm});
        }
        {
            var Q0;
            Q0=makeQuery(id+"F9.imprint","IMPRINT",FACE,{"disambiguationData":[TD([[makeQuery(id+"F9.imprint","IMPRINT",EDGE,{"derivedFrom":sQuery(id+"F9.wireOp",EDGE,"E18.2.2.0")}),1.0]])]});
            extrude(context, id + "F39", {"entities" : qUnion([Q0]), "operationType" : NewBodyOperationType.REMOVE, "oppositeDirection" : true, "depth" : 3 * mm});
        }
        {
            var Q0;
            Q0=makeQuery(id+"F9.imprint","IMPRINT",FACE,{"disambiguationData":[TD([[makeQuery(id+"F9.imprint","IMPRINT",EDGE,{"derivedFrom":sQuery(id+"F9.wireOp",EDGE,"E18.3.2.0")}),1.0]])]});
            extrude(context, id + "F40", {"entities" : qUnion([Q0]), "operationType" : NewBodyOperationType.REMOVE, "oppositeDirection" : true, "depth" : 4 * mm});
        }
        {
            var Q0;
            Q0=makeQuery(id+"F1.opExtrude","CAP_FACE",FACE,{"disambiguationData":[OSD([sQuery(id+"F0.wireOp",EDGE,"E6.top"),sQuery(id+"F0.wireOp",EDGE,"E6.right"),sQuery(id+"F0.wireOp",EDGE,"E8"),sQuery(id+"F0.wireOp",EDGE,"E9")])],"isStart":false});
            var sketch = newSketch(context, id + "F41", { "sketchPlane" : qUnion([Q0])});
            skLineSegment(sketch, "E21", {"start": v(3.4, -3.33) * mm, "end": v(6.72, 11.67) * mm});
            skPoint(sketch, "E21.endSnap0", {"position": v(6.72, -3.33) * mm});
            skSolve(sketch);
        }
        {
            var Q0;
            {var subQ0=sQuery(id+"F41.wireOp",EDGE,"E21");Q0=makeQuery(id+"F41.imprint","IMPRINT",FACE,{"disambiguationData":[TD([[makeQuery(id+"F41.imprint","IMPRINT",EDGE,{"derivedFrom":subQ0}),1.0]])]});}
            extrude(context, id + "F42", {"entities" : qUnion([Q0]), "operationType" : NewBodyOperationType.ADD, "depth" : 3 * mm});
        }
        {
            var Q0;
            Q0=makeQuery(id+"F6.opExtrude","SWEPT_FACE",FACE,{"disambiguationData":[OSD([sQuery(id+"F5.wireOp",EDGE,"E14.0")])]});
            var sketch = newSketch(context, id + "F43", { "sketchPlane" : qUnion([Q0])});
            skLineSegment(sketch, "E22", {"start": v(9.88, 0) * mm, "end": v(-5.06, -25) * mm});
            skSolve(sketch);
        }
        {
            var Q0;
            {var subQ0=sQuery(id+"F43.wireOp",EDGE,"E22");Q0=makeQuery(id+"F43.imprint","IMPRINT",FACE,{"disambiguationData":[TD([[makeQuery(id+"F43.imprint","IMPRINT",EDGE,{"derivedFrom":subQ0}),1.0]])]});}
            extrude(context, id + "F44", {"entities" : qUnion([Q0]), "operationType" : NewBodyOperationType.ADD, "depth" : 3 * mm});
        }
    });
